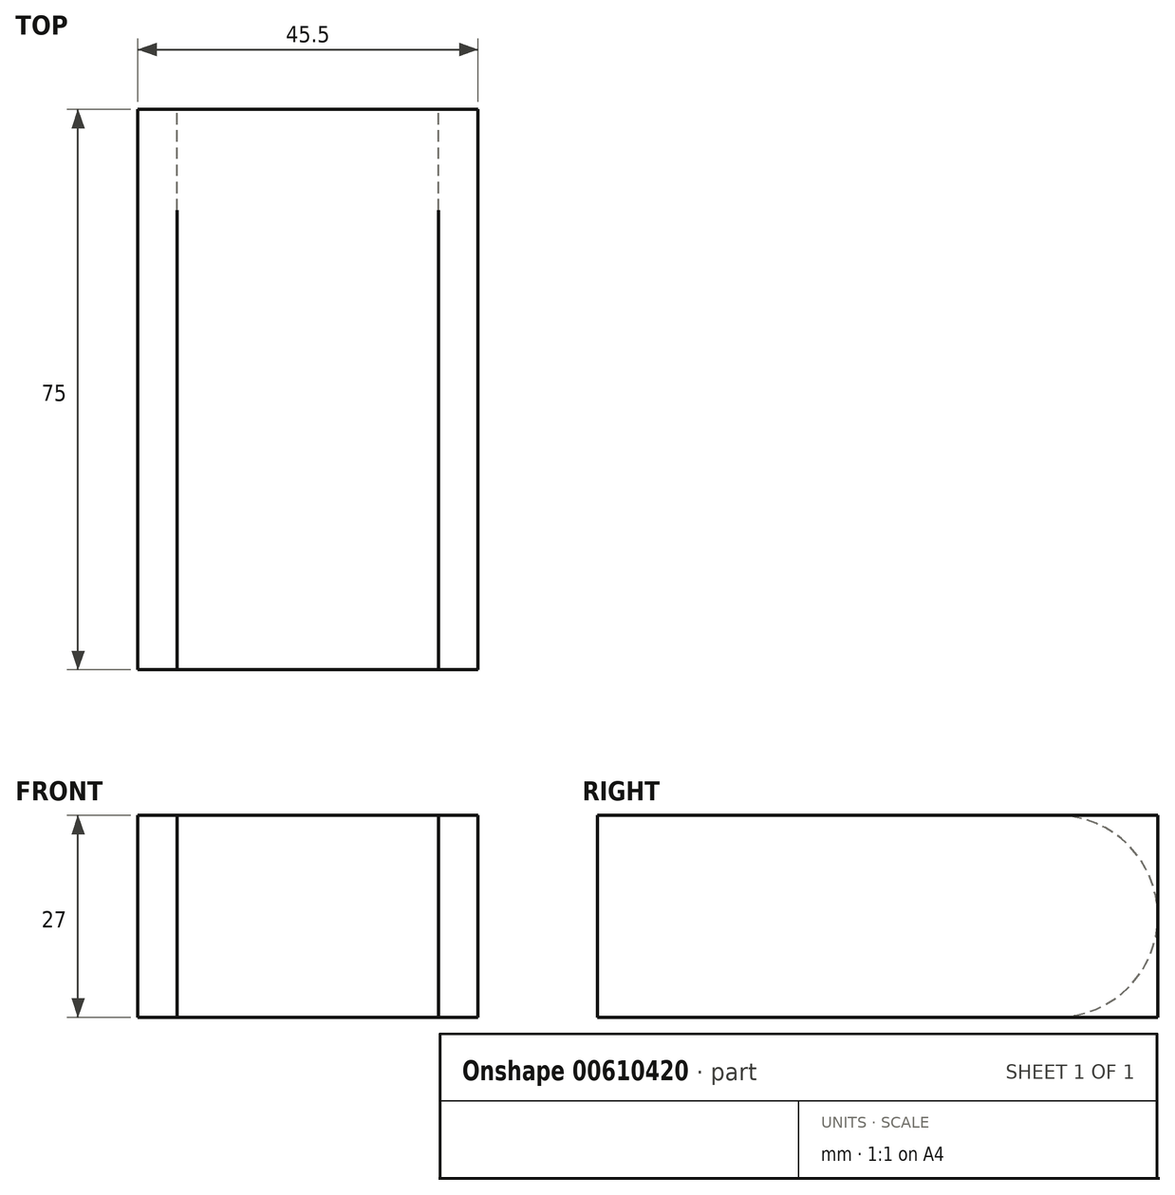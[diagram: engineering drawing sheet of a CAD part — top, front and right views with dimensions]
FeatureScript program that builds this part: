
annotation { "Feature Type Name" : "Feature", "Feature Type Description" : "" }
export const myFeature = defineFeature(function(context is Context, id is Id, definition is map)
    precondition{}
    {
        {
            assignVariable(context, id + "F0", {"name" : "batt_w", "anyValue" : 35 * mm});
        }
        {
            var Q0;
            Q0=qCreatedBy(makeId("Right.planeOp"),FACE);
            var sketch = newSketch(context, id + "F1", { "sketchPlane" : qUnion([Q0])});
            skLineSegment(sketch, "E0.bottom", {"start": v(37.5, -13.5) * mm, "end": v(-37.5, -13.5) * mm});
            skLineSegment(sketch, "E0.top", {"start": v(37.5, 13.5) * mm, "end": v(-37.5, 13.5) * mm});
            skLineSegment(sketch, "E0.left", {"start": v(37.5, -13.5) * mm, "end": v(37.5, 13.5) * mm});
            skLineSegment(sketch, "E0.right", {"start": v(-37.5, -13.5) * mm, "end": v(-37.5, 13.5) * mm});
            skPoint(sketch, "E0.middle", {"position": v(0, 0) * mm});
            skArc(sketch, "E1", {"start": v(24, -13.5) * mm, "mid": v(37.5, 0) * mm, "end": v(24, 13.5) * mm});
            skSolve(sketch);
        }
        {
            var Q0;
            {var subQ4=sQuery(id+"F1.wireOp",EDGE,"E0.right");Q0=makeQuery(id+"F1.imprint","IMPRINT",FACE,{"disambiguationData":[TD([[makeQuery(id+"F1.imprint","IMPRINT",EDGE,{"derivedFrom":subQ4}),-1.0]])]});}
            var Q1;
            {var subQ0=sQuery(id+"F1.wireOp",EDGE,"E0.left");var subQ1=sQuery(id+"F1.wireOp",EDGE,"E0.bottom");var subQ2=makeQuery(id+"F1.imprint","INTERSECT",VERTEX,{"derivedFrom":[subQ1,subQ0]});Q1=makeQuery(id+"F1.imprint","IMPRINT",FACE,{"disambiguationData":[TD([[makeQuery(id+"F1.imprint","IMPRINT",EDGE,{"disambiguationData":[TD([[subQ2,-1.0]])],"derivedFrom":subQ1}),-1.0]])]});}
            var Q2;
            {var subQ0=sQuery(id+"F1.wireOp",EDGE,"E0.left");var subQ1=sQuery(id+"F1.wireOp",EDGE,"E0.top");var subQ2=makeQuery(id+"F1.imprint","INTERSECT",VERTEX,{"derivedFrom":[subQ1,subQ0]});Q2=makeQuery(id+"F1.imprint","IMPRINT",FACE,{"disambiguationData":[TD([[makeQuery(id+"F1.imprint","IMPRINT",EDGE,{"disambiguationData":[TD([[subQ2,-1.0]])],"derivedFrom":subQ1}),1.0]])]});}
            extrude(context, id + "F2", {"entities" : qUnion([Q0, Q1, Q2]), "depth" : getVariable(context, 'batt_w') + 10.5 * mm, "offsetDistance" : 25 * mm, "symmetric" : true});
        }
        {
            var Q0;
            {var subQ4=sQuery(id+"F1.wireOp",EDGE,"E0.right");Q0=makeQuery(id+"F1.imprint","IMPRINT",FACE,{"disambiguationData":[TD([[makeQuery(id+"F1.imprint","IMPRINT",EDGE,{"derivedFrom":subQ4}),-1.0]])]});}
            extrude(context, id + "F3", {"entities" : qUnion([Q0]), "depth" : getVariable(context, 'batt_w'), "offsetDistance" : 25 * mm, "symmetric" : true});
        }
    });
